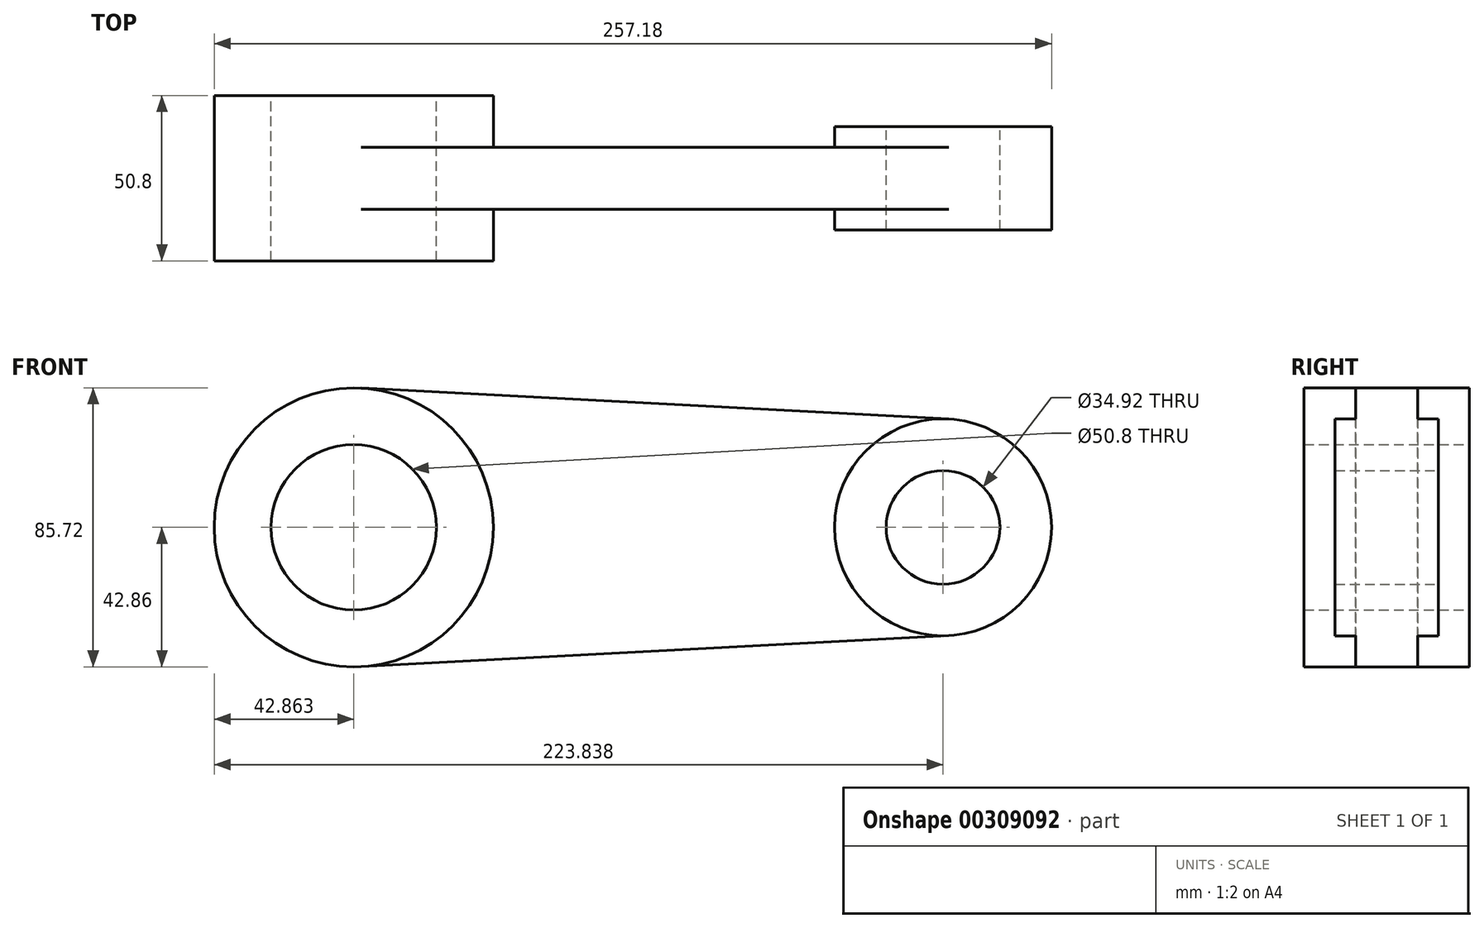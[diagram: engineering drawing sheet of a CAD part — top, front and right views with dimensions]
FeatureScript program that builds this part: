
annotation { "Feature Type Name" : "Feature", "Feature Type Description" : "" }
export const myFeature = defineFeature(function(context is Context, id is Id, definition is map)
    precondition{}
    {
        {
            var Q0;
            Q0=qCreatedBy(makeId("Front.planeOp"),FACE);
            var sketch = newSketch(context, id + "F0", { "sketchPlane" : qUnion([Q0])});
            skCircle(sketch, "E0", {"center": v(-153.25, 0) * mm, "radius": 25.4 * mm});
            skCircle(sketch, "E1", {"center": v(-153.25, 0) * mm, "radius": 42.86 * mm});
            skCircle(sketch, "E2", {"center": v(27.73, 0) * mm, "radius": 17.46 * mm});
            skCircle(sketch, "E3", {"center": v(27.73, 0) * mm, "radius": 33.34 * mm});
            skLineSegment(sketch, "E4", {"start": v(-151, 42.8) * mm, "end": v(29.48, 33.3) * mm});
            skLineSegment(sketch, "E5", {"start": v(-151, -42.8) * mm, "end": v(29.48, -33.3) * mm});
            skSolve(sketch);
        }
        {
            var Q0;
            {var subQ0=sQuery(id+"F0.wireOp",EDGE,"E4");Q0=makeQuery(id+"F0.imprint","IMPRINT",FACE,{"disambiguationData":[TD([[makeQuery(id+"F0.imprint","IMPRINT",EDGE,{"derivedFrom":subQ0}),-1.0]])]});}
            extrude(context, id + "F1", {"entities" : qUnion([Q0]), "endBound" : BoundingType.SYMMETRIC, "depth" : 19.05 * mm});
        }
        {
            var Q0;
            Q0=makeQuery(id+"F0.imprint","IMPRINT",FACE,{"disambiguationData":[TD([[makeQuery(id+"F0.imprint","IMPRINT",EDGE,{"derivedFrom":sQuery(id+"F0.wireOp",EDGE,"E2")}),-1.0]])]});
            extrude(context, id + "F2", {"entities" : qUnion([Q0]), "operationType" : NewBodyOperationType.ADD, "endBound" : BoundingType.SYMMETRIC, "depth" : 31.75 * mm});
        }
        {
            var Q0;
            Q0=makeQuery(id+"F0.imprint","IMPRINT",FACE,{"disambiguationData":[TD([[makeQuery(id+"F0.imprint","IMPRINT",EDGE,{"derivedFrom":sQuery(id+"F0.wireOp",EDGE,"E0")}),-1.0]])]});
            extrude(context, id + "F3", {"entities" : qUnion([Q0]), "operationType" : NewBodyOperationType.ADD, "endBound" : BoundingType.SYMMETRIC, "depth" : 50.8 * mm});
        }
    });
